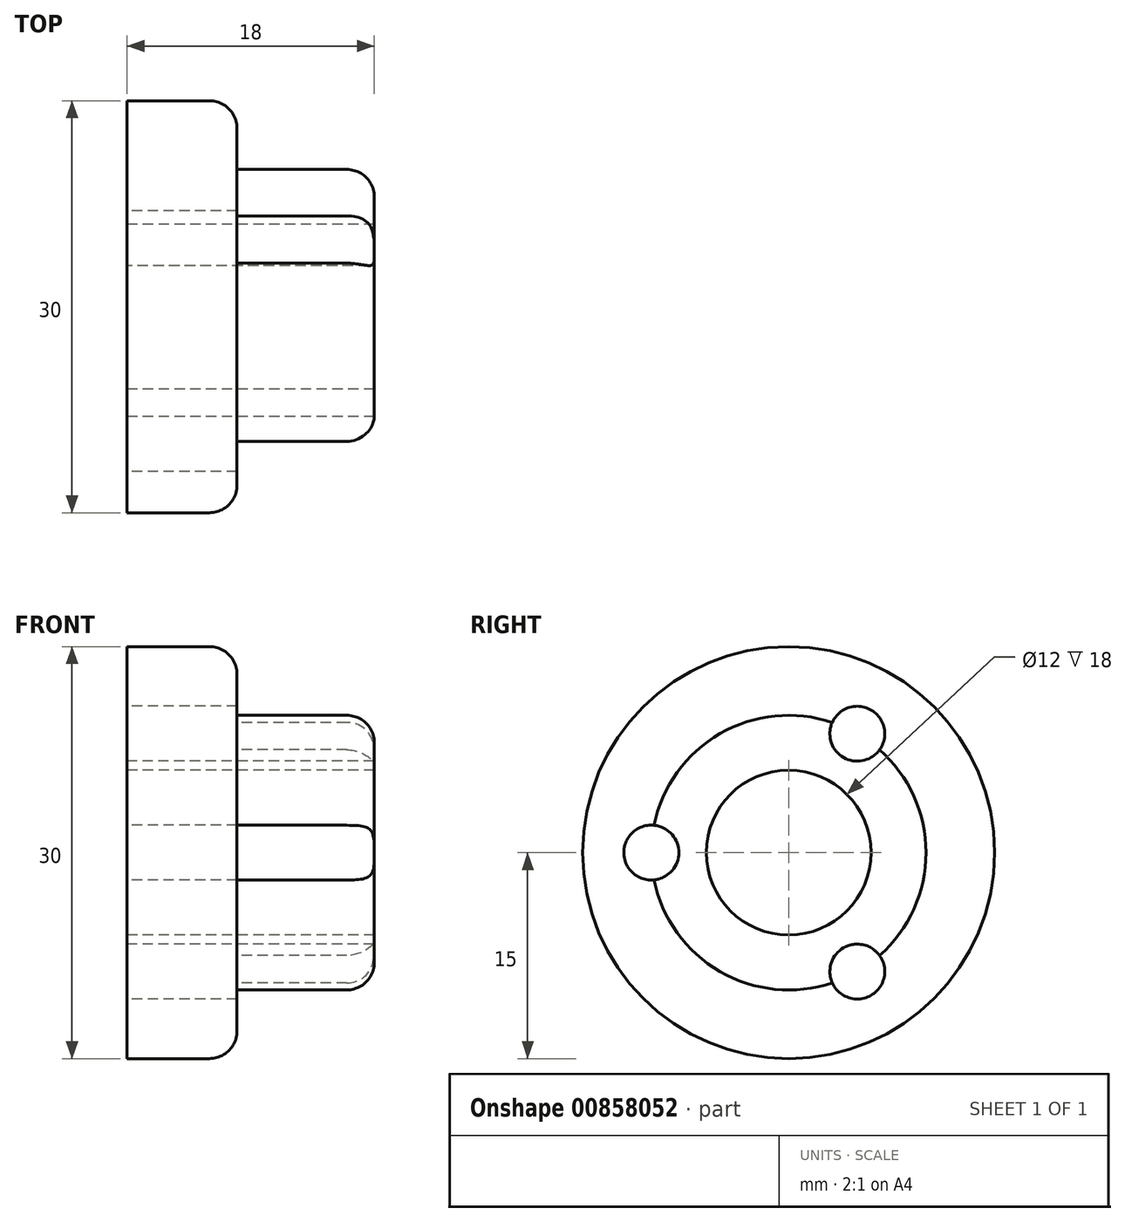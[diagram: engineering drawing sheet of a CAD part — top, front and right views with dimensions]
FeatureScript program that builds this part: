
annotation { "Feature Type Name" : "Feature", "Feature Type Description" : "" }
export const myFeature = defineFeature(function(context is Context, id is Id, definition is map)
    precondition{}
    {
        {
            var Q0;
            Q0=qCreatedBy(makeId("Right.planeOp"),FACE);
            var sketch = newSketch(context, id + "F0", { "sketchPlane" : qUnion([Q0])});
            skCircle(sketch, "E0", {"center": v(0, 0) * mm, "radius": 15 * mm});
            skSolve(sketch);
        }
        {
            var Q0;
            Q0=makeQuery(id+"F0.imprint","IMPRINT",FACE,{"disambiguationData":[TD([[makeQuery(id+"F0.imprint","IMPRINT",EDGE,{"derivedFrom":sQuery(id+"F0.wireOp",EDGE,"E0")}),1.0]])]});
            extrude(context, id + "F1", {"entities" : qUnion([Q0]), "depth" : 8 * mm, "offsetDistance" : 25 * mm});
        }
        {
            var Q0;
            Q0=makeQuery(id+"F1.opExtrude","CAP_FACE",FACE,{"disambiguationData":[OSD([sQuery(id+"F0.wireOp",EDGE,"E0")])],"isStart":false});
            var sketch = newSketch(context, id + "F2", { "sketchPlane" : qUnion([Q0])});
            skCircle(sketch, "E1", {"center": v(0, 0) * mm, "radius": 10 * mm});
            skSolve(sketch);
        }
        {
            var Q0;
            Q0 = qSketchRegion(id + "F2", true);
            extrude(context, id + "F3", {"entities" : qUnion([Q0]), "operationType" : NewBodyOperationType.ADD, "depth" : 10 * mm, "offsetDistance" : 25 * mm});
        }
        {
            var Q0;
            Q0=makeQuery(id+"F1.opExtrude","CAP_FACE",FACE,{"disambiguationData":[OSD([sQuery(id+"F0.wireOp",EDGE,"E0")])],"isStart":true});
            var sketch = newSketch(context, id + "F4", { "sketchPlane" : qUnion([Q0])});
            skPoint(sketch, "E2", {"position": v(0, 0) * mm});
            skSolve(sketch);
        }
        {
            var Q0;
            Q0=sQuery(id+"F4.wireOp",VERTEX,"E2");
            var Q1;
            Q1=makeQuery(id+"F1.opExtrude","SWEPT_BODY",BODY,{"disambiguationData":[OSD([sQuery(id+"F0.wireOp",EDGE,"E0")])]});
            hole(context, id + "F5", {"style" : HoleStyle.SIMPLE, "endStyle" : HoleEndStyle.THROUGH, "standardTappedOrClearance" : lookupTablePath({ "standard" : "Custom", "fit" : "Normal", "size" : "M5", "type" : "Clearance" }), "standardBlindInLast" : lookupTablePath({ "fit" : "Standard", "standard" : "Custom", "size" : "M5", "type" : "Clearance" }), "holeDiameter" : 12 * mm, "majorDiameter" : 5 * mm, "isTappedThrough" : true, "tappedDepth" : 12 * mm, "tapClearance" : 3, "locations" : qUnion([Q0]), "scope" : qUnion([Q1])});
        }
        {
            var Q0;
            Q0=makeQuery(id+"F3.opExtrude","CAP_EDGE",EDGE,{"disambiguationData":[OSD([sQuery(id+"F2.wireOp",EDGE,"E1")])],"isStart":false});
            fillet(context, id + "F6", {"entities" : qUnion([Q0]), "radius" : 2 * mm, "tangentPropagation" : true, "allowEdgeOverflow" : false});
        }
        {
            var Q0;
            Q0=makeQuery(id+"F1.opExtrude","CAP_EDGE",EDGE,{"disambiguationData":[OSD([sQuery(id+"F0.wireOp",EDGE,"E0")])],"isStart":false});
            fillet(context, id + "F7", {"entities" : qUnion([Q0]), "radius" : 2 * mm, "tangentPropagation" : true, "allowEdgeOverflow" : false});
        }
        {
            var Q0;
            Q0=makeQuery(id+"F1.opExtrude","CAP_FACE",FACE,{"disambiguationData":[OSD([sQuery(id+"F0.wireOp",EDGE,"E0")])],"isStart":true});
            var sketch = newSketch(context, id + "F8", { "sketchPlane" : qUnion([Q0])});
            skPoint(sketch, "E3", {"position": v(10, 0) * mm});
            skPoint(sketch, "E4.1.0", {"position": v(-5, 8.66) * mm});
            skPoint(sketch, "E4.2.0", {"position": v(-5, -8.66) * mm});
            skPoint(sketch, "E4.center", {"position": v(0, 0) * mm});
            skSolve(sketch);
        }
        {
            var Q0;
            Q0=sQuery(id+"F8.wireOp",VERTEX,"E4.center");
            var Q1;
            Q1=sQuery(id+"F8.wireOp",VERTEX,"E3");
            var Q2;
            Q2=sQuery(id+"F8.wireOp",VERTEX,"E4.2.0");
            var Q3;
            Q3=sQuery(id+"F8.wireOp",VERTEX,"E4.1.0");
            var Q4;
            Q4=makeQuery(id+"F1.opExtrude","SWEPT_BODY",BODY,{"disambiguationData":[OSD([sQuery(id+"F0.wireOp",EDGE,"E0")])]});
            hole(context, id + "F9", {"style" : HoleStyle.SIMPLE, "endStyle" : HoleEndStyle.THROUGH, "holeDiameter" : 4 * mm, "majorDiameter" : 5 * mm, "isTappedThrough" : true, "tappedDepth" : 12 * mm, "tapClearance" : 3, "locations" : qUnion([Q0, Q1, Q2, Q3]), "scope" : qUnion([Q4])});
        }
    });
